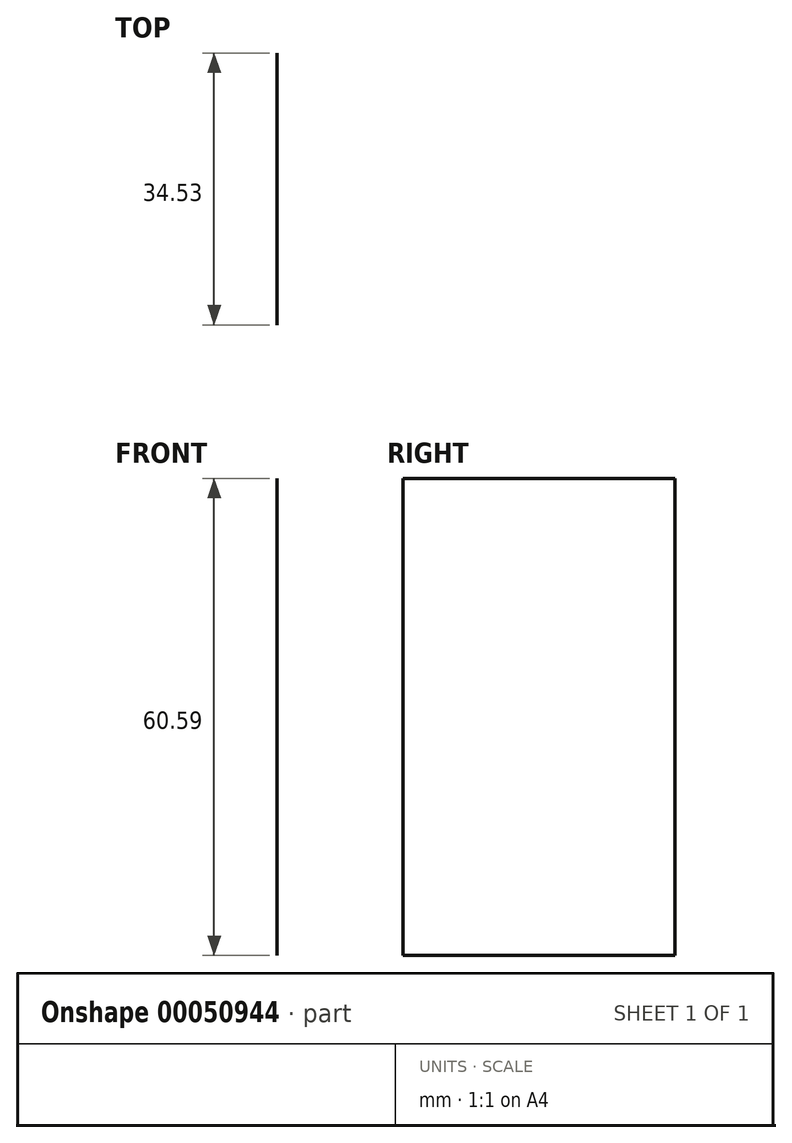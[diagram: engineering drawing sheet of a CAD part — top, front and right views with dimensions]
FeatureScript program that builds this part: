
annotation { "Feature Type Name" : "Feature", "Feature Type Description" : "" }
export const myFeature = defineFeature(function(context is Context, id is Id, definition is map)
    precondition{}
    {
        {
            var Q0;
            Q0=qCreatedBy(makeId("Front.planeOp"),FACE);
            var sketch = newSketch(context, id + "F0", { "sketchPlane" : qUnion([Q0])});
            skLineSegment(sketch, "E0", {"start": v(-60.4, -58.56) * mm, "end": v(-60.4, 2.03) * mm});
            skSolve(sketch);
        }
        {
            var Q0;
            Q0=sQuery(id+"F0.wireOp",EDGE,"E0");
            extrude(context, id + "F1", {"bodyType" : ToolBodyType.SURFACE, "surfaceEntities" : qUnion([Q0]), "depth" : 34.53 * mm});
        }
    });
